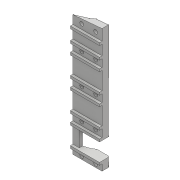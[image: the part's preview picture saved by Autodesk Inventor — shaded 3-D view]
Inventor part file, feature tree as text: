
AUTODESK INVENTOR PART (.ipt)
format: ipt  version: 2017 (Build 210142000, 142)  size: 232,960 bytes
history: native  units: mm
features: extrude x7, sketch x7, plane x1, fillet x1
ambient origin geometry x8: Origin, YZ Plane, XZ Plane, XY Plane, X Axis, Y Axis, Z Axis, Center Point
bodies: Solid1 (feature_tree)
feature tree (16):
  extrude  "Extrusion1"  Depth=18.0mm
  extrude  "Extrusion6"  Depth=21.0mm
  extrude  "Extrusion7"  Depth=21.0mm
  plane  "Work Plane2"
  extrude  "Extrusion8"  Depth=23.0mm
  extrude  "Extrusion9"  Depth=10.0mm
  extrude  "Extrusion10"  TaperAngle=150.0deg  [1 undecoded]
  fillet  "Fillet1"  Radius=100.0mm
  extrude  "Extrusion12"  Depth=14.0mm
  sketch  "Sketch1"  dims[d0=114.0mm d1=18.0mm]
  sketch  "Sketch6"  dims[d2=9.0mm d3=21.0mm]
  sketch  "Sketch7"  dims[d4=10.5mm d5=21.0mm]
  sketch  "Sketch8"  dims[d6=100.0mm d7=0.0mm d37=23.0mm]
  sketch  "Sketch9"  dims[d38=6.0mm d39=10.0mm]
  sketch  "Sketch10"  dims[d40=4.0mm d41=150.0deg d42=100.0mm d43=0.0mm]
  sketch  "Sketch12"  dims[d44=8.0mm d45=59.5mm d46=90.0deg d47=30.543262mm d48=100.0mm d49=0.0mm d50=8.0mm d51=80.5mm d52=21.0mm d53=55.0mm d54=18.0mm d55=100.0mm d56=0.0mm d57=2.0mm d58=2.0mm d59=2.0mm d60=2.0mm d61=2.0mm d62=2.0mm d63=2.0mm d64=2.0mm d65=2.0mm d66=0.0mm d67=3.0mm d68=3.0mm d69=3.0mm d70=3.0mm d71=3.0mm d72=3.0mm d73=3.0mm d74=3.0mm d75=3.0mm d76=3.0mm d77=2.0mm d78=0.0mm d79=1.0mm d84=18.0mm d85=6.0mm d86=14.0mm d87=0.0mm]
note: 1 required parameter value undecoded (feature->parameter linkage not recoverable at this tier; creation-order binding heuristic only, values carry confidence <= 0.55)
